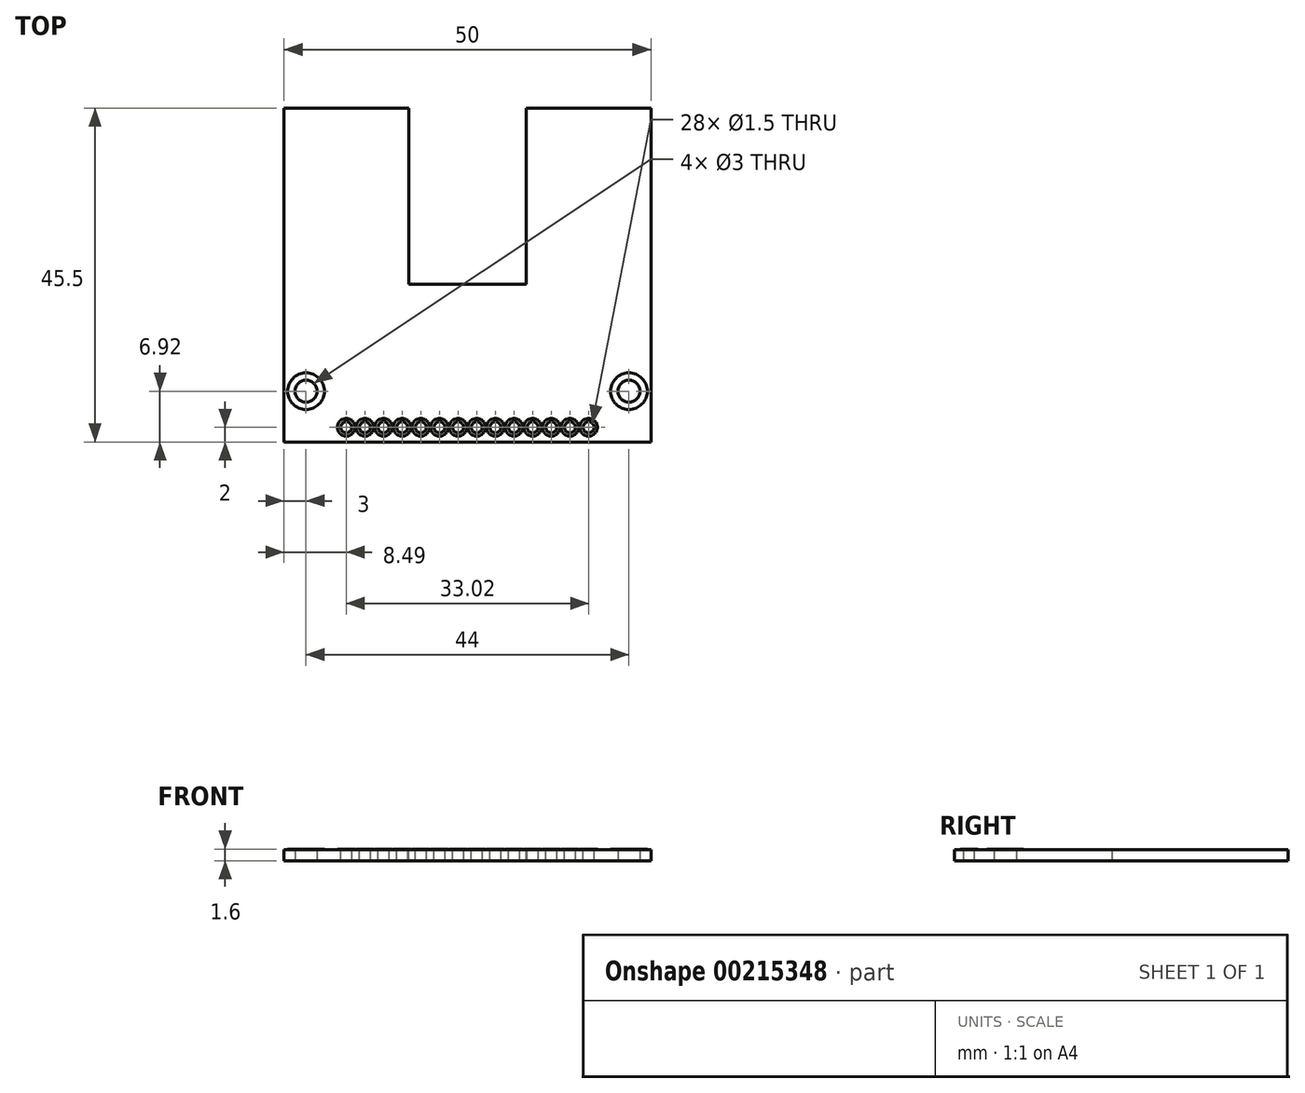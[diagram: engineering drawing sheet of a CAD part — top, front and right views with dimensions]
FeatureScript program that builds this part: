
annotation { "Feature Type Name" : "Feature", "Feature Type Description" : "" }
export const myFeature = defineFeature(function(context is Context, id is Id, definition is map)
    precondition{}
    {
        {
            var Q0;
            Q0=qCreatedBy(makeId("Top.planeOp"),FACE);
            var sketch = newSketch(context, id + "F0", { "sketchPlane" : qUnion([Q0])});
            skLineSegment(sketch, "E0.bottom", {"start": v(-25, 43) * mm, "end": v(25, 43) * mm});
            skLineSegment(sketch, "E0.top", {"start": v(-25, -43) * mm, "end": v(25, -43) * mm});
            skLineSegment(sketch, "E0.left", {"start": v(-25, 43) * mm, "end": v(-25, -43) * mm});
            skLineSegment(sketch, "E0.right", {"start": v(25, 43) * mm, "end": v(25, -43) * mm});
            skPoint(sketch, "E0.middle", {"position": v(0, 0) * mm});
            skCircle(sketch, "E1", {"center": v(-22, 40) * mm, "radius": 1.5 * mm});
            skCircle(sketch, "E2", {"center": v(22, 40) * mm, "radius": 1.5 * mm});
            skCircle(sketch, "E3", {"center": v(-22, -36.08) * mm, "radius": 1.5 * mm});
            skCircle(sketch, "E4", {"center": v(22, -36.08) * mm, "radius": 1.5 * mm});
            skSolve(sketch);
        }
        {
            var Q0;
            Q0=qSketchRegion(id+"F0",true);
            extrude(context, id + "F1", {"entities" : qUnion([Q0]), "depth" : 1.5 * mm});
        }
        {
            var Q0;
            Q0=makeQuery(id+"F1.opExtrude","CAP_FACE",FACE,{"disambiguationData":[OSD([sQuery(id+"F0.wireOp",EDGE,"E0.bottom"),sQuery(id+"F0.wireOp",EDGE,"E0.top"),sQuery(id+"F0.wireOp",EDGE,"E0.left"),sQuery(id+"F0.wireOp",EDGE,"E0.right"),sQuery(id+"F0.wireOp",EDGE,"E1"),sQuery(id+"F0.wireOp",EDGE,"E2"),sQuery(id+"F0.wireOp",EDGE,"E3"),sQuery(id+"F0.wireOp",EDGE,"E4")])],"isStart":false});
            var sketch = newSketch(context, id + "F2", { "sketchPlane" : qUnion([Q0])});
            skCircle(sketch, "E5", {"center": v(-16.51, -41) * mm, "radius": 0.75 * mm});
            skCircle(sketch, "E6.1.0.0", {"center": v(-13.97, -41) * mm, "radius": 0.75 * mm});
            skCircle(sketch, "E6.2.0.0", {"center": v(-11.43, -41) * mm, "radius": 0.75 * mm});
            skCircle(sketch, "E6.3.0.0", {"center": v(-8.9, -41) * mm, "radius": 0.75 * mm});
            skCircle(sketch, "E6.4.0.0", {"center": v(-6.35, -41) * mm, "radius": 0.75 * mm});
            skCircle(sketch, "E6.5.0.0", {"center": v(-3.81, -41) * mm, "radius": 0.75 * mm});
            skCircle(sketch, "E6.6.0.0", {"center": v(-1.27, -41) * mm, "radius": 0.75 * mm});
            skCircle(sketch, "E6.7.0.0", {"center": v(1.27, -41) * mm, "radius": 0.75 * mm});
            skCircle(sketch, "E6.8.0.0", {"center": v(3.8, -41) * mm, "radius": 0.75 * mm});
            skCircle(sketch, "E6.9.0.0", {"center": v(6.35, -41) * mm, "radius": 0.75 * mm});
            skCircle(sketch, "E6.10.0.0", {"center": v(8.89, -41) * mm, "radius": 0.75 * mm});
            skCircle(sketch, "E6.11.0.0", {"center": v(11.43, -41) * mm, "radius": 0.75 * mm});
            skCircle(sketch, "E6.12.0.0", {"center": v(13.97, -41) * mm, "radius": 0.75 * mm});
            skCircle(sketch, "E6.13.0.0", {"center": v(16.5, -41) * mm, "radius": 0.75 * mm});
            skLineSegment(sketch, "E6.direction1", {"start": v(-16.51, -41) * mm, "end": v(-13.97, -41) * mm, "construction": true});
            skCircle(sketch, "E7", {"center": v(-3.8, 40) * mm, "radius": 0.75 * mm});
            skCircle(sketch, "E8.1.0.0", {"center": v(-1.27, 40) * mm, "radius": 0.75 * mm});
            skCircle(sketch, "E8.2.0.0", {"center": v(1.27, 40) * mm, "radius": 0.75 * mm});
            skCircle(sketch, "E8.3.0.0", {"center": v(3.81, 40) * mm, "radius": 0.75 * mm});
            skSolve(sketch);
        }
        {
            var Q0;
            Q0=qSketchRegion(id+"F2",true);
            extrude(context, id + "F3", {"entities" : qUnion([Q0]), "operationType" : NewBodyOperationType.REMOVE, "endBound" : BoundingType.THROUGH_ALL, "oppositeDirection" : true, "depth" : 25 * mm});
        }
        {
            var Q0;
            Q0=makeQuery(id+"F1.opExtrude","CAP_FACE",FACE,{"disambiguationData":[OSD([sQuery(id+"F0.wireOp",EDGE,"E0.bottom"),sQuery(id+"F0.wireOp",EDGE,"E0.top"),sQuery(id+"F0.wireOp",EDGE,"E0.left"),sQuery(id+"F0.wireOp",EDGE,"E0.right"),sQuery(id+"F0.wireOp",EDGE,"E1"),sQuery(id+"F0.wireOp",EDGE,"E2"),sQuery(id+"F0.wireOp",EDGE,"E3"),sQuery(id+"F0.wireOp",EDGE,"E4")])],"isStart":false});
            var sketch = newSketch(context, id + "F4", { "sketchPlane" : qUnion([Q0])});
            skLineSegment(sketch, "E9.bottom", {"start": v(-23, 2.5) * mm, "end": v(23, 2.5) * mm});
            skLineSegment(sketch, "E9.top", {"start": v(-23, 36.5) * mm, "end": v(23, 36.5) * mm});
            skLineSegment(sketch, "E9.left", {"start": v(-23, 2.5) * mm, "end": v(-23, 36.5) * mm});
            skLineSegment(sketch, "E9.right", {"start": v(23, 2.5) * mm, "end": v(23, 36.5) * mm});
            skPoint(sketch, "E9.middle", {"position": v(0, 19.5) * mm});
            skSolve(sketch);
        }
        {
            var Q0;
            Q0 = qSketchRegion(id + "F4", true);
            extrude(context, id + "F5", {"entities" : qUnion([Q0]), "operationType" : NewBodyOperationType.REMOVE, "endBound" : BoundingType.THROUGH_ALL, "oppositeDirection" : true, "depth" : 25 * mm});
        }
        {
            var Q0;
            Q0=makeQuery(id+"F1.opExtrude","CAP_FACE",FACE,{"disambiguationData":[OSD([sQuery(id+"F0.wireOp",EDGE,"E0.bottom"),sQuery(id+"F0.wireOp",EDGE,"E0.top"),sQuery(id+"F0.wireOp",EDGE,"E0.left"),sQuery(id+"F0.wireOp",EDGE,"E0.right"),sQuery(id+"F0.wireOp",EDGE,"E1"),sQuery(id+"F0.wireOp",EDGE,"E2"),sQuery(id+"F0.wireOp",EDGE,"E3"),sQuery(id+"F0.wireOp",EDGE,"E4")])],"isStart":false});
            var sketch = newSketch(context, id + "F6", { "sketchPlane" : qUnion([Q0])});
            skLineSegment(sketch, "E10.bottom", {"start": v(-25, 43) * mm, "end": v(25, 43) * mm});
            skLineSegment(sketch, "E10.top", {"start": v(-25, 2.5) * mm, "end": v(25, 2.5) * mm});
            skLineSegment(sketch, "E10.left", {"start": v(-25, 43) * mm, "end": v(-25, 2.5) * mm});
            skLineSegment(sketch, "E10.right", {"start": v(25, 43) * mm, "end": v(25, 2.5) * mm});
            skSolve(sketch);
        }
        {
            var Q0;
            Q0 = qSketchRegion(id + "F6", true);
            extrude(context, id + "F7", {"entities" : qUnion([Q0]), "operationType" : NewBodyOperationType.REMOVE, "oppositeDirection" : true, "depth" : 25 * mm});
        }
        {
            var Q0;
            Q0=makeQuery(id+"F1.opExtrude","CAP_FACE",FACE,{"disambiguationData":[OSD([sQuery(id+"F0.wireOp",EDGE,"E0.bottom"),sQuery(id+"F0.wireOp",EDGE,"E0.top"),sQuery(id+"F0.wireOp",EDGE,"E0.left"),sQuery(id+"F0.wireOp",EDGE,"E0.right"),sQuery(id+"F0.wireOp",EDGE,"E1"),sQuery(id+"F0.wireOp",EDGE,"E2"),sQuery(id+"F0.wireOp",EDGE,"E3"),sQuery(id+"F0.wireOp",EDGE,"E4")])],"isStart":false});
            var sketch = newSketch(context, id + "F8", { "sketchPlane" : qUnion([Q0])});
            skCircle(sketch, "E11", {"center": v(-22, -36.08) * mm, "radius": 2.5 * mm});
            skCircle(sketch, "E12", {"center": v(22, -36.08) * mm, "radius": 2.5 * mm});
            skCircle(sketch, "E13", {"center": v(-22, -36.08) * mm, "radius": 1.5 * mm});
            skCircle(sketch, "E14", {"center": v(22, -36.08) * mm, "radius": 1.5 * mm});
            skSolve(sketch);
        }
        {
            var Q0;
            Q0 = qSketchRegion(id + "F8", true);
            extrude(context, id + "F9", {"entities" : qUnion([Q0]), "depth" : 0.1 * mm});
        }
        {
            var Q0;
            Q0=makeQuery(id+"F1.opExtrude","CAP_FACE",FACE,{"disambiguationData":[OSD([sQuery(id+"F0.wireOp",EDGE,"E0.bottom"),sQuery(id+"F0.wireOp",EDGE,"E0.top"),sQuery(id+"F0.wireOp",EDGE,"E0.left"),sQuery(id+"F0.wireOp",EDGE,"E0.right"),sQuery(id+"F0.wireOp",EDGE,"E1"),sQuery(id+"F0.wireOp",EDGE,"E2"),sQuery(id+"F0.wireOp",EDGE,"E3"),sQuery(id+"F0.wireOp",EDGE,"E4")])],"isStart":false});
            var sketch = newSketch(context, id + "F10", { "sketchPlane" : qUnion([Q0])});
            skCircle(sketch, "E15", {"center": v(-16.51, -41) * mm, "radius": 1.2 * mm});
            skCircle(sketch, "E16", {"center": v(-16.51, -41) * mm, "radius": 0.75 * mm});
            skCircle(sketch, "E17.1.0.0", {"center": v(-13.97, -41) * mm, "radius": 0.75 * mm});
            skCircle(sketch, "E17.1.0.1", {"center": v(-13.97, -41) * mm, "radius": 1.2 * mm});
            skCircle(sketch, "E17.2.0.0", {"center": v(-11.43, -41) * mm, "radius": 0.75 * mm});
            skCircle(sketch, "E17.2.0.1", {"center": v(-11.43, -41) * mm, "radius": 1.2 * mm});
            skCircle(sketch, "E17.3.0.0", {"center": v(-8.9, -41) * mm, "radius": 0.75 * mm});
            skCircle(sketch, "E17.3.0.1", {"center": v(-8.9, -41) * mm, "radius": 1.2 * mm});
            skCircle(sketch, "E17.4.0.0", {"center": v(-6.35, -41) * mm, "radius": 0.75 * mm});
            skCircle(sketch, "E17.4.0.1", {"center": v(-6.35, -41) * mm, "radius": 1.2 * mm});
            skCircle(sketch, "E17.5.0.0", {"center": v(-3.81, -41) * mm, "radius": 0.75 * mm});
            skCircle(sketch, "E17.5.0.1", {"center": v(-3.81, -41) * mm, "radius": 1.2 * mm});
            skCircle(sketch, "E17.6.0.0", {"center": v(-1.27, -41) * mm, "radius": 0.75 * mm});
            skCircle(sketch, "E17.6.0.1", {"center": v(-1.27, -41) * mm, "radius": 1.2 * mm});
            skCircle(sketch, "E17.7.0.0", {"center": v(1.27, -41) * mm, "radius": 0.75 * mm});
            skCircle(sketch, "E17.7.0.1", {"center": v(1.27, -41) * mm, "radius": 1.2 * mm});
            skCircle(sketch, "E17.8.0.0", {"center": v(3.8, -41) * mm, "radius": 0.75 * mm});
            skCircle(sketch, "E17.8.0.1", {"center": v(3.8, -41) * mm, "radius": 1.2 * mm});
            skCircle(sketch, "E17.9.0.0", {"center": v(6.35, -41) * mm, "radius": 0.75 * mm});
            skCircle(sketch, "E17.9.0.1", {"center": v(6.35, -41) * mm, "radius": 1.2 * mm});
            skCircle(sketch, "E17.10.0.0", {"center": v(8.89, -41) * mm, "radius": 0.75 * mm});
            skCircle(sketch, "E17.10.0.1", {"center": v(8.89, -41) * mm, "radius": 1.2 * mm});
            skCircle(sketch, "E17.11.0.0", {"center": v(11.43, -41) * mm, "radius": 0.75 * mm});
            skCircle(sketch, "E17.11.0.1", {"center": v(11.43, -41) * mm, "radius": 1.2 * mm});
            skCircle(sketch, "E17.12.0.0", {"center": v(13.97, -41) * mm, "radius": 0.75 * mm});
            skCircle(sketch, "E17.12.0.1", {"center": v(13.97, -41) * mm, "radius": 1.2 * mm});
            skCircle(sketch, "E17.13.0.0", {"center": v(16.51, -41) * mm, "radius": 0.75 * mm});
            skCircle(sketch, "E17.13.0.1", {"center": v(16.51, -41) * mm, "radius": 1.2 * mm});
            skLineSegment(sketch, "E17.direction1", {"start": v(-16.51, -41) * mm, "end": v(-13.97, -41) * mm, "construction": true});
            skSolve(sketch);
        }
        {
            var Q0;
            Q0 = qSketchRegion(id + "F10", true);
            extrude(context, id + "F11", {"entities" : qUnion([Q0]), "depth" : 0.1 * mm});
        }
        {
            var Q0;
            Q0=makeQuery(id+"F1.opExtrude","CAP_FACE",FACE,{"disambiguationData":[OSD([sQuery(id+"F0.wireOp",EDGE,"E0.bottom"),sQuery(id+"F0.wireOp",EDGE,"E0.top"),sQuery(id+"F0.wireOp",EDGE,"E0.left"),sQuery(id+"F0.wireOp",EDGE,"E0.right"),sQuery(id+"F0.wireOp",EDGE,"E1"),sQuery(id+"F0.wireOp",EDGE,"E2"),sQuery(id+"F0.wireOp",EDGE,"E3"),sQuery(id+"F0.wireOp",EDGE,"E4")])],"isStart":false});
            var sketch = newSketch(context, id + "F12", { "sketchPlane" : qUnion([Q0])});
            skLineSegment(sketch, "E18.bottom", {"start": v(-8, 2.5) * mm, "end": v(8, 2.5) * mm});
            skLineSegment(sketch, "E18.top", {"start": v(-8, -21.5) * mm, "end": v(8, -21.5) * mm});
            skLineSegment(sketch, "E18.left", {"start": v(-8, 2.5) * mm, "end": v(-8, -21.5) * mm});
            skLineSegment(sketch, "E18.right", {"start": v(8, 2.5) * mm, "end": v(8, -21.5) * mm});
            skPoint(sketch, "E18.middle", {"position": v(0, -9.5) * mm});
            skSolve(sketch);
        }
        {
            var Q0;
            Q0 = qSketchRegion(id + "F12", true);
            extrude(context, id + "F13", {"entities" : qUnion([Q0]), "operationType" : NewBodyOperationType.REMOVE, "oppositeDirection" : true, "depth" : 25 * mm});
        }
    });
